# Revit family: PLAFOLED
name_source: partatom
category: Luminaires
units: mm (PartAtom-declared; Revit-internal decimal feet)

## family parameters
Cote de connecteur circulaire = Utiliser le diamètre
Couper avec des vides une fois chargée = Oui
Hôte = Face
Numéro OmniClass = 23.80.70.11.14.11
Partagée = Oui
Point de calcul de pièce = Oui
Source d'éclairage = Oui
Titre OmniClass = Downlights
Type d'élément = Normal

## types (4) — shared parameters
Angle de l'inclinaison = 60.00°
Emettre la visibilité des formes dans le rendu = Non
Emettre à partir du diamètre du cercle = 610 mm
Fabricant = Résistex
Filtre de couleur = 16777215
Garantie = 5 ans
Gradation des changements de température de couleur de lampe = <Aucun>
IK = 08
IP = 40
Image du type = <Aucun>
Indice de charge = Eclairage
Matériau corps = PC Blanc
Matériau diffuseur = PC Transparent
Modèle = Plafoled
Nombre pôles = 1
Tension = 230 V
URL = https://www.resistex-sa.com
Épaisseur = 35 mm  [stored 0.114829 ft]
Épaisseur diffuseur = 2 mm  [stored 0.00656168 ft]
zero-valued in all types: Elévation par défaut

## per-type parameters (varying)
| type | Charge apparente | Commentaires relatifs à la puissance | Coût | Description | Diamètre | Diamètre collerette | Fichier de distribution photométrique |
| 759203 | 20 VA | 18.8W | 67.5 $ | Plafonnier équipé d'un module LED SMD, efficacité lumineuse de 75.6lm/W | 240 mm  [stored 0.787402 ft] | 192 mm | 759203.ies |
| 759204 | 20 VA | 18.8W | 67.5 $ | Plafonnier équipé d'un module LED SMD, efficacité lumineuse de 80.8lm/W | 240 mm  [stored 0.787402 ft] | 192 mm | 759204.ies |
| 759363 | 34 VA | 33.6W | 110 $ | Plafonnier équipé d'un module LED SMD, efficacité lumineuse de 81.5lm/W | 320 mm  [stored 1.04987 ft] | 272 mm | 759363.ies |
| 759364 | 34 VA | 33.6W | 110 $ | Plafonnier équipé d'un module LED SMD, efficacité lumineuse de 85.6lm/W | 320 mm  [stored 1.04987 ft] | 272 mm | 759364.ies |

note: [stored X ft] marks values corroborated as IEEE doubles in the binary element streams (Revit-internal decimal feet)
